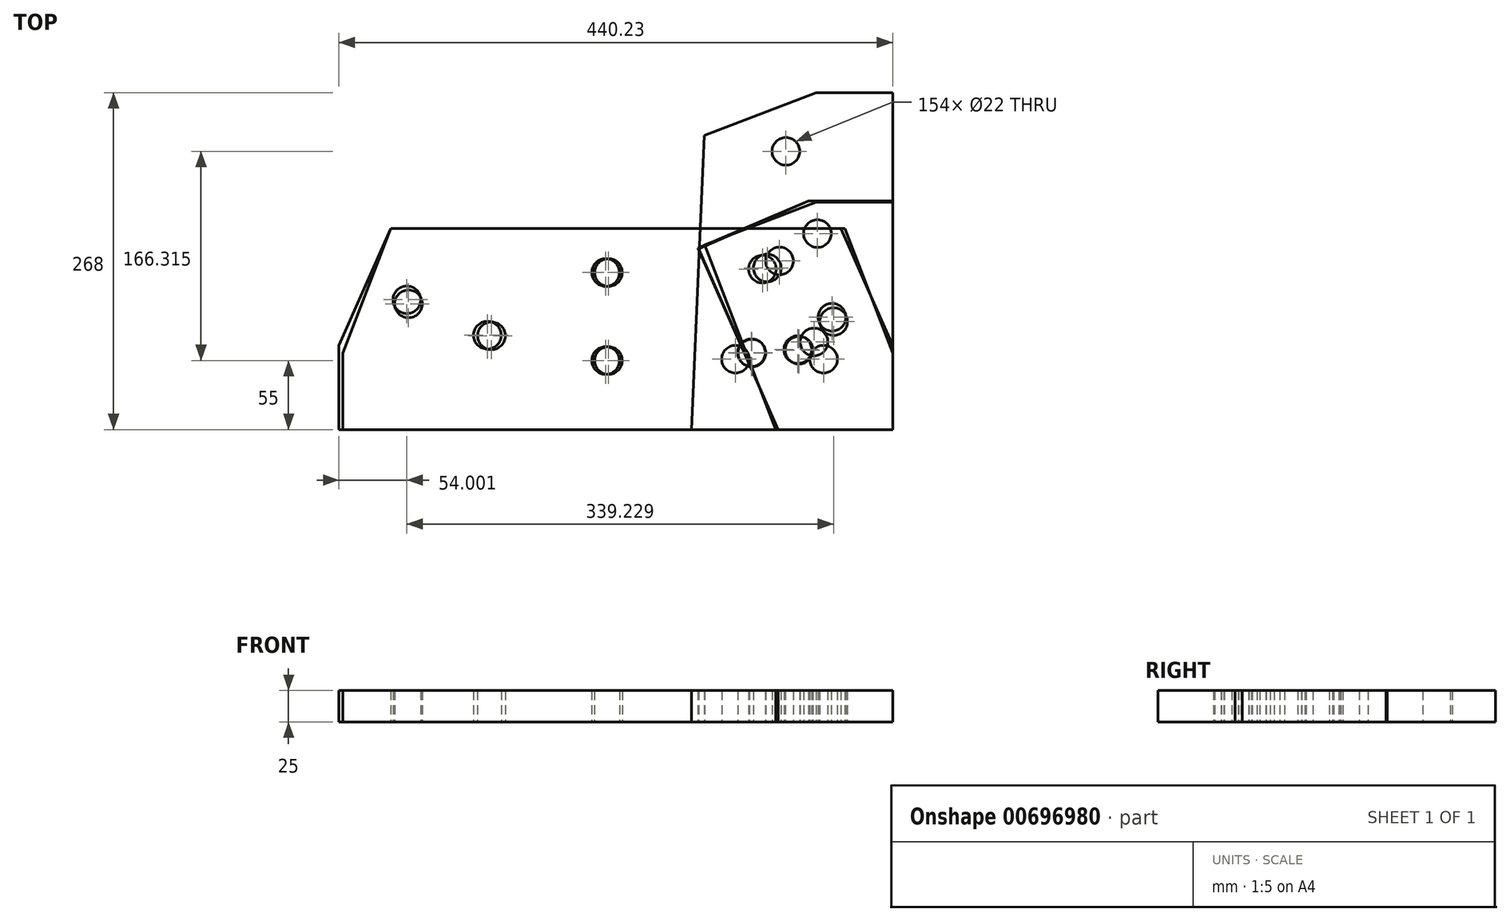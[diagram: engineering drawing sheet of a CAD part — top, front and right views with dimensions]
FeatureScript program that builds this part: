
annotation { "Feature Type Name" : "Feature", "Feature Type Description" : "" }
export const myFeature = defineFeature(function(context is Context, id is Id, definition is map)
    precondition{}
    {
        {
            var Q0;
            Q0=qCreatedBy(makeId("Top.planeOp"),FACE);
            var sketch = newSketch(context, id + "F0", { "sketchPlane" : qUnion([Q0])});
            skLineSegment(sketch, "E0", {"start": v(0, 0) * mm, "end": v(0, 268) * mm});
            skLineSegment(sketch, "E1", {"start": v(0, 268) * mm, "end": v(-61, 268) * mm});
            skLineSegment(sketch, "E2", {"start": v(-61, 268) * mm, "end": v(-149.7, 233.96) * mm});
            skLineSegment(sketch, "E3", {"start": v(-149.7, 233.96) * mm, "end": v(-160, 0) * mm});
            skLineSegment(sketch, "E4", {"start": v(-160, 0) * mm, "end": v(0, 0) * mm});
            skCircle(sketch, "E5", {"center": v(-84.95, 221.31) * mm, "radius": 11 * mm});
            skCircle(sketch, "E6", {"center": v(-59.87, 155.96) * mm, "radius": 11 * mm});
            skCircle(sketch, "E7", {"center": v(-125, 56) * mm, "radius": 11 * mm});
            skCircle(sketch, "E8", {"center": v(-55, 56) * mm, "radius": 11 * mm});
            skSolve(sketch);
        }
        {
            var Q0;
            Q0 = qSketchRegion(id + "F0", true);
            extrude(context, id + "F1", {"entities" : qUnion([Q0]), "depth" : 25 * mm, "offsetDistance" : 25 * mm});
        }
        {
            var Q0;
            Q0=qCreatedBy(makeId("Top.planeOp"),FACE);
            var sketch = newSketch(context, id + "F2", { "sketchPlane" : qUnion([Q0])});
            skLineSegment(sketch, "E9", {"start": v(0, 0) * mm, "end": v(-93, 0) * mm});
            skLineSegment(sketch, "E10", {"start": v(-93, 0) * mm, "end": v(-149.63, 146.8) * mm});
            skLineSegment(sketch, "E11", {"start": v(-149.63, 146.8) * mm, "end": v(-61, 181) * mm});
            skLineSegment(sketch, "E12", {"start": v(-61, 181) * mm, "end": v(0, 181) * mm});
            skLineSegment(sketch, "E13", {"start": v(0, 181) * mm, "end": v(0, 0) * mm});
            skCircle(sketch, "E14", {"center": v(-99.72, 128.55) * mm, "radius": 11 * mm});
            skCircle(sketch, "E15", {"center": v(-74.52, 63.24) * mm, "radius": 11 * mm});
            skSolve(sketch);
        }
        {
            var Q0;
            Q0 = qSketchRegion(id + "F2", true);
            extrude(context, id + "F3", {"entities" : qUnion([Q0]), "depth" : 25 * mm, "offsetDistance" : 25 * mm});
        }
        {
            var Q0;
            Q0=qCreatedBy(makeId("Top.planeOp"),FACE);
            var sketch = newSketch(context, id + "F4", { "sketchPlane" : qUnion([Q0])});
            skLineSegment(sketch, "E16", {"start": v(0, 0) * mm, "end": v(-437, 0) * mm});
            skLineSegment(sketch, "E17", {"start": v(-437, 0) * mm, "end": v(-437, 61) * mm});
            skLineSegment(sketch, "E18", {"start": v(-437, 61) * mm, "end": v(-399, 160) * mm});
            skLineSegment(sketch, "E19", {"start": v(-399, 160) * mm, "end": v(-38, 160) * mm});
            skLineSegment(sketch, "E20", {"start": v(-38, 160) * mm, "end": v(0, 61) * mm});
            skLineSegment(sketch, "E21", {"start": v(0, 61) * mm, "end": v(0, 0) * mm});
            skCircle(sketch, "E22", {"center": v(-385, 100) * mm, "radius": 11 * mm});
            skCircle(sketch, "E23", {"center": v(-319, 74.66) * mm, "radius": 11 * mm});
            skCircle(sketch, "E24", {"center": v(-112, 60.9) * mm, "radius": 11 * mm});
            skCircle(sketch, "E25", {"center": v(-47, 85.85) * mm, "radius": 11 * mm});
            skCircle(sketch, "E26", {"center": v(-226, 125) * mm, "radius": 11 * mm});
            skCircle(sketch, "E27", {"center": v(-226, 55) * mm, "radius": 11 * mm});
            skSolve(sketch);
        }
        {
            var Q0;
            Q0 = qSketchRegion(id + "F4", true);
            extrude(context, id + "F5", {"entities" : qUnion([Q0]), "depth" : 25 * mm, "offsetDistance" : 25 * mm});
        }
        {
            var Q0;
            Q0=qCreatedBy(makeId("Top.planeOp"),FACE);
            var sketch = newSketch(context, id + "F6", { "sketchPlane" : qUnion([Q0])});
            skLineSegment(sketch, "E28", {"start": v(0, 0) * mm, "end": v(-91, 0) * mm});
            skLineSegment(sketch, "E29", {"start": v(-91, 0) * mm, "end": v(-154.76, 144.56) * mm});
            skLineSegment(sketch, "E30", {"start": v(-154.76, 144.56) * mm, "end": v(-67, 182) * mm});
            skLineSegment(sketch, "E31", {"start": v(-67, 182) * mm, "end": v(0, 182) * mm});
            skLineSegment(sketch, "E32", {"start": v(0, 182) * mm, "end": v(0, 0) * mm});
            skCircle(sketch, "E33", {"center": v(-90.04, 134.12) * mm, "radius": 11 * mm});
            skCircle(sketch, "E34", {"center": v(-62.58, 69.73) * mm, "radius": 11 * mm});
            skSolve(sketch);
        }
        {
            var Q0;
            Q0 = qSketchRegion(id + "F6", true);
            extrude(context, id + "F7", {"entities" : qUnion([Q0]), "depth" : 25 * mm, "offsetDistance" : 25 * mm});
        }
        {
            var Q0;
            Q0=qCreatedBy(makeId("Top.planeOp"),FACE);
            var sketch = newSketch(context, id + "F8", { "sketchPlane" : qUnion([Q0])});
            skLineSegment(sketch, "E35", {"start": v(0, 0) * mm, "end": v(-91, 0) * mm});
            skLineSegment(sketch, "E36", {"start": v(-91, 0) * mm, "end": v(-154.36, 143.65) * mm});
            skLineSegment(sketch, "E37", {"start": v(-154.36, 143.65) * mm, "end": v(-67, 182) * mm});
            skLineSegment(sketch, "E38", {"start": v(-67, 182) * mm, "end": v(0, 182) * mm});
            skLineSegment(sketch, "E39", {"start": v(0, 182) * mm, "end": v(0, 0) * mm});
            skCircle(sketch, "E40", {"center": v(-103.6, 127.7) * mm, "radius": 11 * mm});
            skCircle(sketch, "E41", {"center": v(-75.47, 63.6) * mm, "radius": 11 * mm});
            skSolve(sketch);
        }
        {
            var Q0;
            Q0 = qSketchRegion(id + "F8", true);
            extrude(context, id + "F9", {"entities" : qUnion([Q0]), "depth" : 25 * mm, "offsetDistance" : 25 * mm});
        }
        {
            var Q0;
            Q0=qCreatedBy(makeId("Top.planeOp"),FACE);
            var sketch = newSketch(context, id + "F10", { "sketchPlane" : qUnion([Q0])});
            skLineSegment(sketch, "E42", {"start": v(0, 0) * mm, "end": v(-440.23, 0) * mm});
            skLineSegment(sketch, "E43", {"start": v(-440.23, 0) * mm, "end": v(-440.23, 67) * mm});
            skLineSegment(sketch, "E44", {"start": v(-440.23, 67) * mm, "end": v(-399.21, 160) * mm});
            skLineSegment(sketch, "E45", {"start": v(-399.21, 160) * mm, "end": v(-41.21, 160) * mm});
            skLineSegment(sketch, "E46", {"start": v(-41.21, 160) * mm, "end": v(0, 67) * mm});
            skLineSegment(sketch, "E47", {"start": v(0, 67) * mm, "end": v(0, 0) * mm});
            skCircle(sketch, "E48", {"center": v(-48.23, 89.45) * mm, "radius": 11 * mm});
            skCircle(sketch, "E49", {"center": v(-112.23, 61.22) * mm, "radius": 11 * mm});
            skCircle(sketch, "E50", {"center": v(-322.23, 75.07) * mm, "radius": 11 * mm});
            skCircle(sketch, "E51", {"center": v(-386.23, 103.3) * mm, "radius": 11 * mm});
            skCircle(sketch, "E52", {"center": v(-228.23, 125) * mm, "radius": 11 * mm});
            skCircle(sketch, "E53", {"center": v(-228.23, 55) * mm, "radius": 11 * mm});
            skSolve(sketch);
        }
        {
            var Q0;
            Q0 = qSketchRegion(id + "F10", true);
            extrude(context, id + "F11", {"entities" : qUnion([Q0]), "depth" : 25 * mm, "offsetDistance" : 25 * mm});
        }
    });
